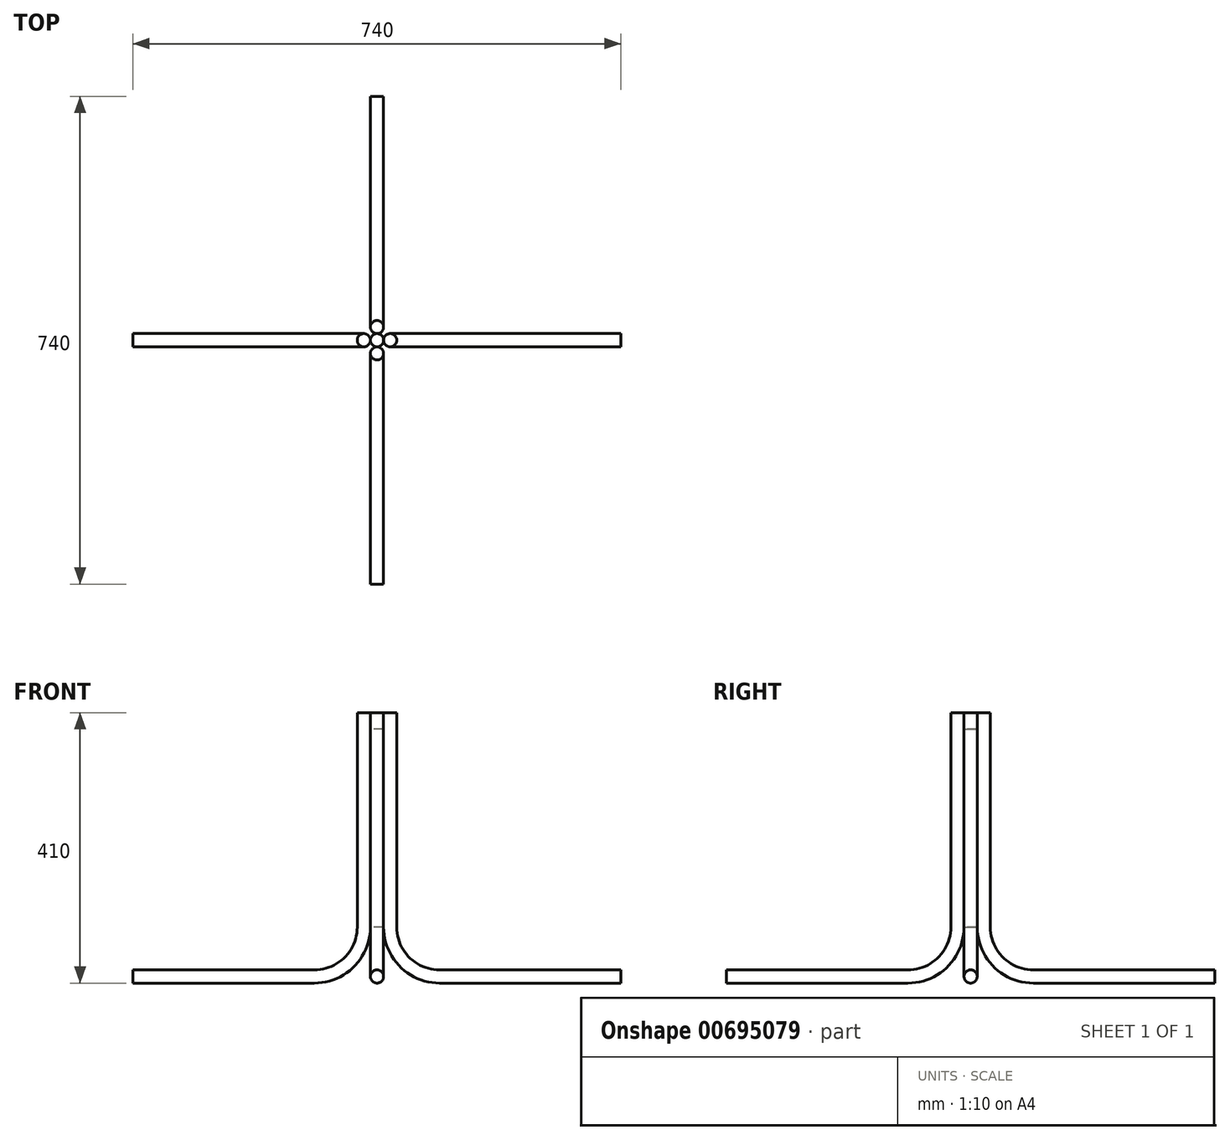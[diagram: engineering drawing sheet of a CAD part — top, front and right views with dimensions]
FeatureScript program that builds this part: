
annotation { "Feature Type Name" : "Feature", "Feature Type Description" : "" }
export const myFeature = defineFeature(function(context is Context, id is Id, definition is map)
    precondition{}
    {
        {
            var Q0;
            Q0=qCreatedBy(makeId("Front.planeOp"),FACE);
            var sketch = newSketch(context, id + "F0", { "sketchPlane" : qUnion([Q0])});
            skLineSegment(sketch, "E0", {"start": v(-370, 0) * mm, "end": v(-95, 0) * mm});
            skArc(sketch, "E1", {"start": v(-95, 0) * mm, "mid": v(-41.97, 21.97) * mm, "end": v(-20, 75) * mm});
            skLineSegment(sketch, "E2", {"start": v(-20, 75) * mm, "end": v(-20, 400) * mm});
            skSolve(sketch);
        }
        {
            var Q0;
            Q0=qCreatedBy(makeId("Right.planeOp"),FACE);
            var Q1;
            Q1=sQuery(id+"F0.wireOp",VERTEX,"E0.start");
            cPlane(context, id + "F1", {"entities" : qUnion([Q0, Q1]), "cplaneType" : CPlaneType.PLANE_POINT, "offset" : 277 * mm, "oppositeDirection" : true, "width" : 150 * mm, "height" : 150 * mm});
        }
        {
            var Q0;
            Q0=qCreatedBy(id+"F1.planeOp",FACE);
            var sketch = newSketch(context, id + "F2", { "sketchPlane" : qUnion([Q0])});
            skCircle(sketch, "E3", {"center": v(0, 0) * mm, "radius": 10 * mm});
            skSolve(sketch);
        }
        {
            var Q0;
            Q0=makeQuery(id+"F2.imprint","IMPRINT",FACE,{"disambiguationData":[TD([[makeQuery(id+"F2.imprint","IMPRINT",EDGE,{"derivedFrom":sQuery(id+"F2.wireOp",EDGE,"E3")}),1.0]])]});
            var Q1;
            Q1 = qConstructionFilter(qBodyType(qCreatedBy(id + "F0" ,EDGE), BodyType.WIRE), ConstructionObject.NO);
            sweep(context, id + "F3", {"profiles" : qUnion([Q0]), "path" : qUnion([Q1])});
        }
        {
            var Q0;
            Q0=qCreatedBy(makeId("Right.planeOp"),FACE);
            var sketch = newSketch(context, id + "F4", { "sketchPlane" : qUnion([Q0])});
            skLineSegment(sketch, "E4", {"start": v(0, 0) * mm, "end": v(0, 194.97) * mm, "construction": true});
            skSolve(sketch);
        }
        {
            var Q0;
            Q0=makeQuery(id+"F3.opSweep","SWEPT_BODY",BODY,{"disambiguationData":[OSD([sQuery(id+"F0.wireOp",EDGE,"E2"),sQuery(id+"F2.wireOp",EDGE,"E3")])]});
            var Q1;
            Q1=sQuery(id+"F4.wireOp",EDGE,"E4");
            circularPattern(context, id + "F5", {"entities" : qUnion([Q0]), "axis" : qUnion([Q1]), "angle" : 360 * degree, "instanceCount" : 4, "equalSpace" : true});
        }
        {
            var Q0;
            Q0=qCreatedBy(makeId("Top.planeOp"),FACE);
            cPlane(context, id + "F6", {"entities" : qUnion([Q0]), "cplaneType" : CPlaneType.OFFSET, "offset" : 75 * mm, "width" : 150 * mm, "height" : 150 * mm});
        }
        {
            var Q0;
            Q0=qCreatedBy(id+"F6.planeOp",FACE);
            var sketch = newSketch(context, id + "F7", { "sketchPlane" : qUnion([Q0])});
            skCircle(sketch, "E5", {"center": v(0, 0) * mm, "radius": 10 * mm});
            skSolve(sketch);
        }
        {
            var Q0;
            Q0=makeQuery(id+"F7.imprint","IMPRINT",FACE,{"disambiguationData":[TD([[makeQuery(id+"F7.imprint","IMPRINT",EDGE,{"derivedFrom":sQuery(id+"F7.wireOp",EDGE,"E5")}),1.0]])]});
            var Q1;
            Q1=makeQuery(id+"F5.opPattern","COPY",FACE,{"derivedFrom":makeQuery(id+"F3.opSweep","CAP_FACE",FACE,{"disambiguationData":[OSD([sQuery(id+"F0.wireOp",VERTEX,"E2.end"),sQuery(id+"F2.wireOp",EDGE,"E3")])],"isStart":false}),"instanceName":"2"});
            extrude(context, id + "F8", {"entities" : qUnion([Q0]), "endBound" : BoundingType.UP_TO_SURFACE, "depth" : 25 * mm, "endBoundEntityFace" : qUnion([Q1]), "hasOffset" : true, "offsetDistance" : 25 * mm});
        }
    });
